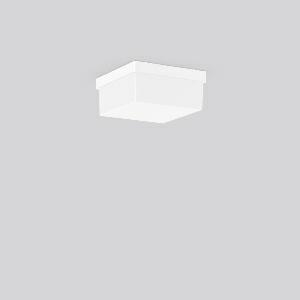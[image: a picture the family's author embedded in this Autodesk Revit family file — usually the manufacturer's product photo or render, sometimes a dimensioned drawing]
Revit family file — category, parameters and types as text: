
# Revit family: quadrat_22146_002_8208
name_source: partatom
category: Lighting Fixtures
units: mm (PartAtom-declared; Revit-internal decimal feet)

## family parameters
Cut with Voids When Loaded = No
Host = Face
Light Source = No
Part Type = Normal
Room Calculation Point = No
Round Connector Dimension = Use Diameter
Shared = No

## types (1)
- QUADRAT (1 x QA60/clear E27, 915 lm, 57 W, 3000)
    Apparent Load = 57 VA
    CIE Flux Codes = 35 64 85 77 54
    Color Rendering = 90
    Color Temperature = 3000
    Default Elevation = 1800 mm
    Description = Series: QUADRAT
Square surface-mounted luminaire in classic design. Base: plastic. Diffuser: plastic (polypropylene), opal, satin finish. Diffuser fastening: spring system. Suitable for Ceiling mounting, Wall (surface). IP 43 ceiling mounting, IP 44 wall mounting. 
Colour: white
Length: 226 mm
Width: 226 mm
Height: 110 mm
Lamp: A60
Number of lamps: 1
Wattage: 75 W
Socket: E27
System power: 17 W
Rated luminous flux: 490 lm
Luminous efficiency: 29 lm/W
Control gear: Converter not necessary
Protection class: II
Type of protection: IP 43
    Height = 110 mm
    Lamp = 1 x QA60/clear E27
    Lamp Light Flux = 915 lm
    Lamp Power = 57 W
    Lamp count = 1
    Length = 226 mm
    Lifetime = 3000 h
    Luminous efficacy = 9 lm/W
    Manufacturer = RZB
    ModVariant = No
    Model = 22146.002
    Mounting Place = Ceiling, Wall
    Mounting Type = Surface mounted
    Number of Poles = 1
    OnlyDefault = Yes
    Power Factor = 1
    Product Name = QUADRAT
    Product group = Surface mounted ceiling and wall luminaires
    ProductGroupID = 305
    Protection Class = Protection class II
    Protection Degree = IP 43
    RLX_Detail_Level = 1
    RLX_Emergency_Light_Flux = 0 lm
    RLX_Emergency_Type = 0
    RLX_Emergency_Type_DB = No
    RlxData = <blob elided: 8985 chars, md5=a841ea36>
    Socket = E27
    Standby Power = 0 W
    System Light Flux = 495 lm
    System Power = 57 W
    Type Comments = Product without accessories
    Type Image = 22146.002.jpg
    URL = http://relux.com
    VarID = ---
    Voltage = 230 V
    Voltage Range = 220-240 V
    Weight = 0.00 kg
    Width = 226 mm

## geometry (parser evidence)
native form markers: Sweep x10
no freeform markers — native parametric forms only
